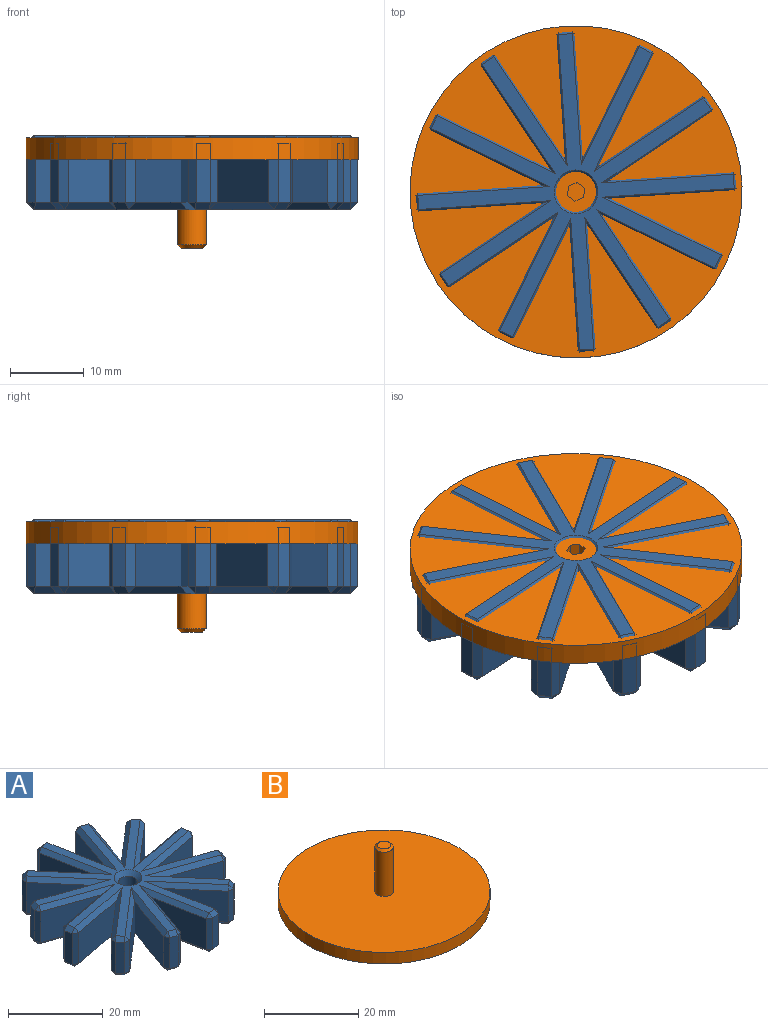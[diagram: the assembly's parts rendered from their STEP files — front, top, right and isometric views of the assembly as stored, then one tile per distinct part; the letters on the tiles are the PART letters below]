
ASSEMBLY  parts=2 mates=1
PART A: 185 faces, bbox 44.4x44.4x10 mm
  f0: plane 10.69x9.19mm, normal (-0.65,0.76,0), area 112.8mm2, adj f36,f41,f49,f50
  f1: plane 8x1.46mm, normal (-0.76,-0.65,0), area 15.4mm2, adj f48,f49,f59,f60
  f2: plane 10.69x9.19mm, normal (0.65,-0.76,0), area 112.8mm2, adj f3,f58,f59,f69
  f3: plane 13.3x8mm, normal (-0.94,0.33,0), area 112.8mm2, adj f2,f63,f73,f74
  f4: plane 8x1.81mm, normal (-0.33,-0.94,0), area 15.4mm2, adj f72,f73,f83,f84
  f5: plane 13.3x8mm, normal (0.94,-0.33,0), area 112.8mm2, adj f6,f82,f83,f93
  f6: plane 13.85x8mm, normal (-0.98,-0.19,0), area 112.8mm2, adj f5,f87,f97,f98
  f7: plane 8x1.89mm, normal (0.19,-0.98,0), area 15.4mm2, adj f96,f97,f107,f108
  f8: plane 13.85x8mm, normal (0.98,0.19,0), area 112.8mm2, adj f9,f106,f107,f117
  f9: plane 10.69x9.19mm, normal (-0.76,-0.65,0), area 112.8mm2, adj f8,f111,f121,f122
  f10: plane 8x1.46mm, normal (0.65,-0.76,0), area 15.4mm2, adj f120,f121,f131,f132
  f11: plane 10.69x9.19mm, normal (0.76,0.65,0), area 112.8mm2, adj f12,f130,f131,f141
  f12: plane 13.3x8mm, normal (-0.33,-0.94,0), area 112.8mm2, adj f11,f135,f145,f146
  f13: plane 8x1.81mm, normal (0.94,-0.33,0), area 15.4mm2, adj f144,f145,f155,f156
  f14: plane 13.3x8mm, normal (0.33,0.94,0), area 112.8mm2, adj f15,f154,f155,f166
  f15: plane 13.85x8mm, normal (0.19,-0.98,0), area 112.8mm2, adj f14,f159,f171,f172
  f16: plane 8x1.89mm, normal (0.98,0.19,0), area 15.4mm2, adj f170,f171,f178,f179
  f17: plane 13.85x8mm, normal (-0.19,0.98,0), area 112.8mm2, adj f18,f169,f178,f182
  f18: plane 10.69x9.19mm, normal (0.65,-0.76,0), area 112.8mm2, adj f17,f164,f174,f180
  f19: plane 8x1.46mm, normal (0.76,0.65,0), area 15.4mm2, adj f162,f163,f173,f174
  f20: plane 10.69x9.19mm, normal (-0.65,0.76,0), area 112.8mm2, adj f21,f153,f161,f162
  f21: plane 13.3x8mm, normal (0.94,-0.33,0), area 112.8mm2, adj f20,f148,f149,f157
  f22: plane 8x1.81mm, normal (0.33,0.94,0), area 15.4mm2, adj f138,f139,f147,f148
  f23: plane 13.3x8mm, normal (-0.94,0.33,0), area 112.8mm2, adj f24,f129,f137,f138
  f24: plane 13.85x8mm, normal (0.98,0.19,0), area 112.8mm2, adj f23,f124,f125,f133
  f25: plane 8x1.89mm, normal (-0.19,0.98,0), area 15.4mm2, adj f114,f115,f123,f124
  f26: plane 13.85x8mm, normal (-0.98,-0.19,0), area 112.8mm2, adj f27,f105,f113,f114
  f27: plane 10.69x9.19mm, normal (0.76,0.65,0), area 112.8mm2, adj f26,f100,f101,f109
  f28: plane 8x1.46mm, normal (-0.65,0.76,0), area 15.4mm2, adj f90,f91,f99,f100
  f29: plane 10.69x9.19mm, normal (-0.76,-0.65,0), area 112.8mm2, adj f30,f81,f89,f90
  f30: plane 13.3x8mm, normal (0.33,0.94,0), area 112.8mm2, adj f29,f76,f77,f85
  f31: plane 8x1.81mm, normal (-0.94,0.33,0), area 15.4mm2, adj f66,f67,f75,f76
  f32: plane 13.3x8mm, normal (-0.33,-0.94,0), area 112.8mm2, adj f33,f57,f65,f66
  f33: plane 13.85x8mm, normal (-0.19,0.98,0), area 112.8mm2, adj f32,f52,f53,f61
  f34: plane 8x1.89mm, normal (-0.98,-0.19,0), area 15.4mm2, adj f42,f43,f51,f52
  f35: cylinder r=1.96mm len=8mm, axis (0,0,1), area 98.6mm2, adj f183,f184
  f36: plane 13.85x8mm, normal (0.19,-0.98,0), area 112.8mm2, adj f0,f39,f42,f45
  f37: plane 42.44x42.44mm, normal (0,0,-1), area 425mm2, adj f39,f41,f43,f48,f53,f57,f58,f63
  f38: plane 42.44x42.44mm, normal (0,0,1), area 425mm2, adj f45,f50,f51,f60,f61,f65,f69,f74
  f39: plane 17.52x4.29mm, normal (0.13,-0.69,-0.71), area 22.6mm2, adj f36,f37,f40,f41
  f40: plane 1.17x1mm, normal (-0.46,-0.67,-0.58), area 0.9mm2, adj f39,f42,f43
  f41: plane 14.17x11.62mm, normal (-0.46,0.54,-0.71), area 22.6mm2, adj f0,f37,f39,f44
  f42: plane 8x1.17mm, normal (-0.56,-0.83,0), area 11.3mm2, adj f34,f36,f40,f46
  f43: plane 2.07x1.34mm, normal (-0.69,-0.13,-0.71), area 2.7mm2, adj f34,f37,f40,f47
  f44: plane 1.41x1mm, normal (-0.81,0.06,-0.58), area 0.9mm2, adj f41,f48,f49
  f45: plane 17.52x4.29mm, normal (0.13,-0.69,0.71), area 22.6mm2, adj f36,f38,f46,f50
  f46: plane 1.17x1mm, normal (-0.46,-0.67,0.58), area 0.9mm2, adj f42,f45,f51
  f47: plane 1.17x1mm, normal (-0.67,0.46,-0.58), area 0.9mm2, adj f43,f52,f53
  f48: plane 2.11x2.01mm, normal (-0.54,-0.46,-0.71), area 2.7mm2, adj f1,f37,f44,f54
  f49: plane 8x1.41mm, normal (-1,0.08,0), area 11.3mm2, adj f0,f1,f44,f55
  f50: plane 14.17x11.62mm, normal (-0.46,0.54,0.71), area 22.6mm2, adj f0,f38,f45,f55
  f51: plane 2.07x1.34mm, normal (-0.69,-0.13,0.71), area 2.7mm2, adj f34,f38,f46,f56
  f52: plane 8x1.17mm, normal (-0.83,0.56,0), area 11.3mm2, adj f33,f34,f47,f56
  f53: plane 17.7x3.6mm, normal (-0.13,0.69,-0.71), area 22.6mm2, adj f33,f37,f47,f57
  f54: plane 1.41x1mm, normal (-0.06,-0.81,-0.58), area 0.9mm2, adj f48,f58,f59
  f55: plane 1.41x1mm, normal (-0.81,0.06,0.58), area 0.9mm2, adj f49,f50,f60
  f56: plane 1.17x1mm, normal (-0.67,0.46,0.58), area 0.9mm2, adj f51,f52,f61
  f57: plane 17.15x5.9mm, normal (-0.23,-0.67,-0.71), area 22.6mm2, adj f32,f37,f53,f62
  f58: plane 13.52x12.38mm, normal (0.46,-0.54,-0.71), area 22.6mm2, adj f2,f37,f54,f63
  f59: plane 8x1.41mm, normal (-0.08,-1,0), area 11.3mm2, adj f1,f2,f54,f64
  f60: plane 2.11x2.01mm, normal (-0.54,-0.46,0.71), area 2.7mm2, adj f1,f38,f55,f64
  f61: plane 17.7x3.6mm, normal (-0.13,0.69,0.71), area 22.6mm2, adj f33,f38,f56,f65
  f62: plane 1.27x1mm, normal (-0.74,-0.35,-0.58), area 0.9mm2, adj f57,f66,f67
  f63: plane 16.82x6.84mm, normal (-0.67,0.23,-0.71), area 22.6mm2, adj f3,f37,f58,f68
  f64: plane 1.41x1mm, normal (-0.06,-0.81,0.58), area 0.9mm2, adj f59,f60,f69
  f65: plane 17.15x5.9mm, normal (-0.23,-0.67,0.71), area 22.6mm2, adj f32,f38,f61,f70
  f66: plane 8x1.27mm, normal (-0.9,-0.43,0), area 11.3mm2, adj f31,f32,f62,f70
  f67: plane 2.14x1.58mm, normal (-0.67,0.23,-0.71), area 2.7mm2, adj f31,f37,f62,f71
  f68: plane 1.27x1mm, normal (-0.74,-0.35,-0.58), area 0.9mm2, adj f63,f72,f73
  f69: plane 13.52x12.38mm, normal (0.46,-0.54,0.71), area 22.6mm2, adj f2,f38,f64,f74
  f70: plane 1.27x1mm, normal (-0.74,-0.35,0.58), area 0.9mm2, adj f65,f66,f75
  f71: plane 1.27x1mm, normal (-0.35,0.74,-0.58), area 0.9mm2, adj f67,f76,f77
  f72: plane 2.14x1.58mm, normal (-0.23,-0.67,-0.71), area 2.7mm2, adj f4,f37,f68,f78
  f73: plane 8x1.27mm, normal (-0.9,-0.43,0), area 11.3mm2, adj f3,f4,f68,f79
  f74: plane 16.82x6.84mm, normal (-0.67,0.23,0.71), area 22.6mm2, adj f3,f38,f69,f79
  f75: plane 2.14x1.58mm, normal (-0.67,0.23,0.71), area 2.7mm2, adj f31,f38,f70,f80
  f76: plane 8x1.27mm, normal (-0.43,0.9,0), area 11.3mm2, adj f30,f31,f71,f80
  f77: plane 16.82x6.84mm, normal (0.23,0.67,-0.71), area 22.6mm2, adj f30,f37,f71,f81
  f78: plane 1.27x1mm, normal (0.35,-0.74,-0.58), area 0.9mm2, adj f72,f82,f83
  f79: plane 1.27x1mm, normal (-0.74,-0.35,0.58), area 0.9mm2, adj f73,f74,f84
  f80: plane 1.27x1mm, normal (-0.35,0.74,0.58), area 0.9mm2, adj f75,f76,f85
  f81: plane 13.52x12.38mm, normal (-0.54,-0.46,-0.71), area 22.6mm2, adj f29,f37,f77,f86
  f82: plane 17.15x5.9mm, normal (0.67,-0.23,-0.71), area 22.6mm2, adj f5,f37,f78,f87
  f83: plane 8x1.27mm, normal (0.43,-0.9,0), area 11.3mm2, adj f4,f5,f78,f88
  f84: plane 2.14x1.58mm, normal (-0.23,-0.67,0.71), area 2.7mm2, adj f4,f38,f79,f88
  f85: plane 16.82x6.84mm, normal (0.23,0.67,0.71), area 22.6mm2, adj f30,f38,f80,f89
  f86: plane 1.41x1mm, normal (-0.81,0.06,-0.58), area 0.9mm2, adj f81,f90,f91
  f87: plane 17.7x3.6mm, normal (-0.69,-0.13,-0.71), area 22.6mm2, adj f6,f37,f82,f92
  f88: plane 1.27x1mm, normal (0.35,-0.74,0.58), area 0.9mm2, adj f83,f84,f93
  f89: plane 13.52x12.38mm, normal (-0.54,-0.46,0.71), area 22.6mm2, adj f29,f38,f85,f94
  f90: plane 8x1.41mm, normal (-1,0.08,0), area 11.3mm2, adj f28,f29,f86,f94
  f91: plane 2.11x2.01mm, normal (-0.46,0.54,-0.71), area 2.7mm2, adj f28,f37,f86,f95
  f92: plane 1.17x1mm, normal (-0.46,-0.67,-0.58), area 0.9mm2, adj f87,f96,f97
  f93: plane 17.15x5.9mm, normal (0.67,-0.23,0.71), area 22.6mm2, adj f5,f38,f88,f98
  f94: plane 1.41x1mm, normal (-0.81,0.06,0.58), area 0.9mm2, adj f89,f90,f99
  f95: plane 1.41x1mm, normal (0.06,0.81,-0.58), area 0.9mm2, adj f91,f100,f101
  f96: plane 2.07x1.34mm, normal (0.13,-0.69,-0.71), area 2.7mm2, adj f7,f37,f92,f102
  f97: plane 8x1.17mm, normal (-0.56,-0.83,0), area 11.3mm2, adj f6,f7,f92,f103
  f98: plane 17.7x3.6mm, normal (-0.69,-0.13,0.71), area 22.6mm2, adj f6,f38,f93,f103
  f99: plane 2.11x2.01mm, normal (-0.46,0.54,0.71), area 2.7mm2, adj f28,f38,f94,f104
  f100: plane 8x1.41mm, normal (0.08,1,0), area 11.3mm2, adj f27,f28,f95,f104
  f101: plane 14.17x11.62mm, normal (0.54,0.46,-0.71), area 22.6mm2, adj f27,f37,f95,f105
  f102: plane 1.17x1mm, normal (0.67,-0.46,-0.58), area 0.9mm2, adj f96,f106,f107
  f103: plane 1.17x1mm, normal (-0.46,-0.67,0.58), area 0.9mm2, adj f97,f98,f108
  f104: plane 1.41x1mm, normal (0.06,0.81,0.58), area 0.9mm2, adj f99,f100,f109
  f105: plane 17.52x4.29mm, normal (-0.69,-0.13,-0.71), area 22.6mm2, adj f26,f37,f101,f110
  f106: plane 17.52x4.29mm, normal (0.69,0.13,-0.71), area 22.6mm2, adj f8,f37,f102,f111
  f107: plane 8x1.17mm, normal (0.83,-0.56,0), area 11.3mm2, adj f7,f8,f102,f112
  f108: plane 2.07x1.34mm, normal (0.13,-0.69,0.71), area 2.7mm2, adj f7,f38,f103,f112
  f109: plane 14.17x11.62mm, normal (0.54,0.46,0.71), area 22.6mm2, adj f27,f38,f104,f113
  f110: plane 1.17x1mm, normal (-0.67,0.46,-0.58), area 0.9mm2, adj f105,f114,f115
  f111: plane 14.17x11.62mm, normal (-0.54,-0.46,-0.71), area 22.6mm2, adj f9,f37,f106,f116
  f112: plane 1.17x1mm, normal (0.67,-0.46,0.58), area 0.9mm2, adj f107,f108,f117
  f113: plane 17.52x4.29mm, normal (-0.69,-0.13,0.71), area 22.6mm2, adj f26,f38,f109,f118
  f114: plane 8x1.17mm, normal (-0.83,0.56,0), area 11.3mm2, adj f25,f26,f110,f118
  f115: plane 2.07x1.34mm, normal (-0.13,0.69,-0.71), area 2.7mm2, adj f25,f37,f110,f119
  f116: plane 1.41x1mm, normal (-0.06,-0.81,-0.58), area 0.9mm2, adj f111,f120,f121
  f117: plane 17.52x4.29mm, normal (0.69,0.13,0.71), area 22.6mm2, adj f8,f38,f112,f122
  f118: plane 1.17x1mm, normal (-0.67,0.46,0.58), area 0.9mm2, adj f113,f114,f123
  f119: plane 1.17x1mm, normal (0.46,0.67,-0.58), area 0.9mm2, adj f115,f124,f125
  f120: plane 2.11x2.01mm, normal (0.46,-0.54,-0.71), area 2.7mm2, adj f10,f37,f116,f126
  f121: plane 8x1.41mm, normal (-0.08,-1,0), area 11.3mm2, adj f9,f10,f116,f127
  f122: plane 14.17x11.62mm, normal (-0.54,-0.46,0.71), area 22.6mm2, adj f9,f38,f117,f127
  f123: plane 2.07x1.34mm, normal (-0.13,0.69,0.71), area 2.7mm2, adj f25,f38,f118,f128
  f124: plane 8x1.17mm, normal (0.56,0.83,0), area 11.3mm2, adj f24,f25,f119,f128
  f125: plane 17.7x3.6mm, normal (0.69,0.13,-0.71), area 22.6mm2, adj f24,f37,f119,f129
  f126: plane 1.41x1mm, normal (0.81,-0.06,-0.58), area 0.9mm2, adj f120,f130,f131
  f127: plane 1.41x1mm, normal (-0.06,-0.81,0.58), area 0.9mm2, adj f121,f122,f132
  f128: plane 1.17x1mm, normal (0.46,0.67,0.58), area 0.9mm2, adj f123,f124,f133
  f129: plane 17.15x5.9mm, normal (-0.67,0.23,-0.71), area 22.6mm2, adj f23,f37,f125,f134
  f130: plane 13.52x12.38mm, normal (0.54,0.46,-0.71), area 22.6mm2, adj f11,f37,f126,f135
  f131: plane 8x1.41mm, normal (1,-0.08,0), area 11.3mm2, adj f10,f11,f126,f136
  f132: plane 2.11x2.01mm, normal (0.46,-0.54,0.71), area 2.7mm2, adj f10,f38,f127,f136
  f133: plane 17.7x3.6mm, normal (0.69,0.13,0.71), area 22.6mm2, adj f24,f38,f128,f137
  f134: plane 1.27x1mm, normal (-0.35,0.74,-0.58), area 0.9mm2, adj f129,f138,f139
  f135: plane 16.82x6.84mm, normal (-0.23,-0.67,-0.71), area 22.6mm2, adj f12,f37,f130,f140
  f136: plane 1.41x1mm, normal (0.81,-0.06,0.58), area 0.9mm2, adj f131,f132,f141
  f137: plane 17.15x5.9mm, normal (-0.67,0.23,0.71), area 22.6mm2, adj f23,f38,f133,f142
  f138: plane 8x1.27mm, normal (-0.43,0.9,0), area 11.3mm2, adj f22,f23,f134,f142
  f139: plane 2.14x1.58mm, normal (0.23,0.67,-0.71), area 2.7mm2, adj f22,f37,f134,f143
  f140: plane 1.27x1mm, normal (0.35,-0.74,-0.58), area 0.9mm2, adj f135,f144,f145
  f141: plane 13.52x12.38mm, normal (0.54,0.46,0.71), area 22.6mm2, adj f11,f38,f136,f146
  f142: plane 1.27x1mm, normal (-0.35,0.74,0.58), area 0.9mm2, adj f137,f138,f147
  f143: plane 1.27x1mm, normal (0.74,0.35,-0.58), area 0.9mm2, adj f139,f148,f149
  f144: plane 2.14x1.58mm, normal (0.67,-0.23,-0.71), area 2.7mm2, adj f13,f37,f140,f150
  f145: plane 8x1.27mm, normal (0.43,-0.9,0), area 11.3mm2, adj f12,f13,f140,f151
  f146: plane 16.82x6.84mm, normal (-0.23,-0.67,0.71), area 22.6mm2, adj f12,f38,f141,f151
  f147: plane 2.14x1.58mm, normal (0.23,0.67,0.71), area 2.7mm2, adj f22,f38,f142,f152
  f148: plane 8x1.27mm, normal (0.9,0.43,0), area 11.3mm2, adj f21,f22,f143,f152
  f149: plane 16.82x6.84mm, normal (0.67,-0.23,-0.71), area 22.6mm2, adj f21,f37,f143,f153
  f150: plane 1.27x1mm, normal (0.74,0.35,-0.58), area 0.9mm2, adj f144,f154,f155
  f151: plane 1.27x1mm, normal (0.35,-0.74,0.58), area 0.9mm2, adj f145,f146,f156
  f152: plane 1.27x1mm, normal (0.74,0.35,0.58), area 0.9mm2, adj f147,f148,f157
  f153: plane 13.52x12.38mm, normal (-0.46,0.54,-0.71), area 22.6mm2, adj f20,f37,f149,f158
  f154: plane 17.15x5.9mm, normal (0.23,0.67,-0.71), area 22.6mm2, adj f14,f37,f150,f159
  f155: plane 8x1.27mm, normal (0.9,0.43,0), area 11.3mm2, adj f13,f14,f150,f160
  f156: plane 2.14x1.58mm, normal (0.67,-0.23,0.71), area 2.7mm2, adj f13,f38,f151,f160
  f157: plane 16.82x6.84mm, normal (0.67,-0.23,0.71), area 22.6mm2, adj f21,f38,f152,f161
  f158: plane 1.41x1mm, normal (0.06,0.81,-0.58), area 0.9mm2, adj f153,f162,f163
  f159: plane 17.7x3.6mm, normal (0.13,-0.69,-0.71), area 22.6mm2, adj f15,f37,f154,f165
  f160: plane 1.27x1mm, normal (0.74,0.35,0.58), area 0.9mm2, adj f155,f156,f166
  f161: plane 13.52x12.38mm, normal (-0.46,0.54,0.71), area 22.6mm2, adj f20,f38,f157,f167
  f162: plane 8x1.41mm, normal (0.08,1,0), area 11.3mm2, adj f19,f20,f158,f167
  f163: plane 2.11x2.01mm, normal (0.54,0.46,-0.71), area 2.7mm2, adj f19,f37,f158,f168
  f164: plane 14.17x11.62mm, normal (0.46,-0.54,-0.71), area 22.6mm2, adj f18,f37,f168,f169
  f165: plane 1.17x1mm, normal (0.67,-0.46,-0.58), area 0.9mm2, adj f159,f170,f171
  f166: plane 17.15x5.9mm, normal (0.23,0.67,0.71), area 22.6mm2, adj f14,f38,f160,f172
  f167: plane 1.41x1mm, normal (0.06,0.81,0.58), area 0.9mm2, adj f161,f162,f173
  f168: plane 1.41x1mm, normal (0.81,-0.06,-0.58), area 0.9mm2, adj f163,f164,f174
  f169: plane 17.52x4.29mm, normal (-0.13,0.69,-0.71), area 22.6mm2, adj f17,f37,f164,f175
  f170: plane 2.07x1.34mm, normal (0.69,0.13,-0.71), area 2.7mm2, adj f16,f37,f165,f175
  f171: plane 8x1.17mm, normal (0.83,-0.56,0), area 11.3mm2, adj f15,f16,f165,f176
  f172: plane 17.7x3.6mm, normal (0.13,-0.69,0.71), area 22.6mm2, adj f15,f38,f166,f176
  f173: plane 2.11x2.01mm, normal (0.54,0.46,0.71), area 2.7mm2, adj f19,f38,f167,f177
  f174: plane 8x1.41mm, normal (1,-0.08,0), area 11.3mm2, adj f18,f19,f168,f177
  f175: plane 1.17x1mm, normal (0.46,0.67,-0.58), area 0.9mm2, adj f169,f170,f178
  f176: plane 1.17x1mm, normal (0.67,-0.46,0.58), area 0.9mm2, adj f171,f172,f179
  f177: plane 1.41x1mm, normal (0.81,-0.06,0.58), area 0.9mm2, adj f173,f174,f180
  f178: plane 8x1.17mm, normal (0.56,0.83,0), area 11.3mm2, adj f16,f17,f175,f181
  f179: plane 2.07x1.34mm, normal (0.69,0.13,0.71), area 2.7mm2, adj f16,f38,f176,f181
  f180: plane 14.17x11.62mm, normal (0.46,-0.54,0.71), area 22.6mm2, adj f18,f38,f177,f182
  f181: plane 1.17x1mm, normal (0.46,0.67,0.58), area 0.9mm2, adj f178,f179,f182
  f182: plane 17.52x4.29mm, normal (-0.13,0.69,0.71), area 22.6mm2, adj f17,f38,f180,f181
  f183: cone r=1.96mm half-angle=45deg, axis (0,0,1), area 21.9mm2, adj f35,f38
  f184: cone r=2.96mm half-angle=45deg, axis (0,0,-1), area 21.9mm2, adj f35,f37
PART B: 13 faces, bbox 45x45x15 mm
  f0: plane 45x45mm, normal (0,0,-1), area 1586.2mm2, adj f1,f6,f7,f8,f9,f10,f11
  f1: cylinder r=22.5mm len=45mm, axis (0,0,-1), area 424.1mm2, adj f0,f2
  f2: plane 45x45mm, normal (0,0,1), area 1578.4mm2, adj f1,f3
  f3: cylinder r=1.96mm len=11.5mm, axis (0,0,-1), area 141.7mm2, adj f2,f5
  f4: plane 2.92x2.92mm, normal (0,0,1), area 6.7mm2, adj f5
  f5: cone r=1.46mm half-angle=45deg, axis (0,0,-1), area 7.6mm2, adj f3,f4
  f6: plane 4x1.27mm, normal (0,-1,0), area 5.1mm2, adj f0,f7,f11,f12
  f7: plane 4x1.1mm, normal (0.87,-0.5,0), area 5.1mm2, adj f0,f6,f8,f12
  f8: plane 4x1.1mm, normal (0.87,0.5,0), area 5.1mm2, adj f0,f7,f9,f12
  f9: plane 4x1.27mm, normal (0,1,0), area 5.1mm2, adj f0,f8,f10,f12
  f10: plane 4x1.1mm, normal (-0.87,0.5,0), area 5.1mm2, adj f0,f9,f11,f12
  f11: plane 4x1.1mm, normal (-0.87,-0.5,0), area 5.1mm2, adj f0,f6,f10,f12
  f12: plane 2.54x2.2mm, normal (0,0,-1), area 4.2mm2, adj f6,f7,f8,f9,f10,f11
PLACE A rot(axis=(0,0,-1),6.8deg) t=(-83.65,-37.91,27.24)mm
PLACE B rot(axis=(0.66,-0.75,0),180deg) t=(-83.65,-37.91,26.99)mm
MATE revolute A.f35 <-> B.f3  axis (0,0,1) through (-83.65,-37.91,18.24)mm
